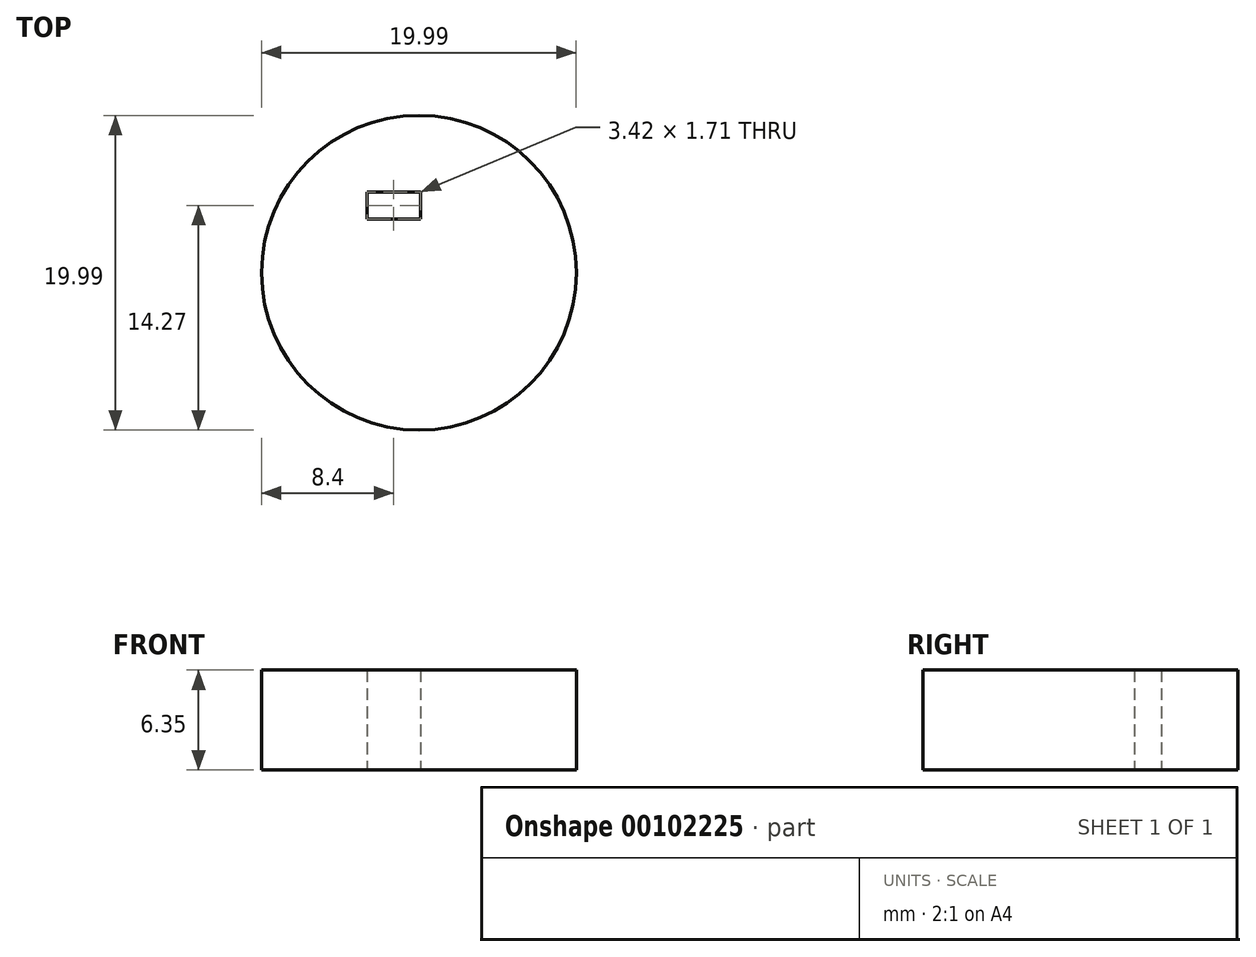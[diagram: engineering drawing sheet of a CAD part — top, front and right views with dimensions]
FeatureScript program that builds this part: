
annotation { "Feature Type Name" : "Feature", "Feature Type Description" : "" }
export const myFeature = defineFeature(function(context is Context, id is Id, definition is map)
    precondition{}
    {
        {
            var Q0;
            Q0=qCreatedBy(makeId("Top.planeOp"),FACE);
            var sketch = newSketch(context, id + "F0", { "sketchPlane" : qUnion([Q0])});
            skCircle(sketch, "E0", {"center": v(13, -19.54) * mm, "radius": 10 * mm});
            skLineSegment(sketch, "E1.bottom", {"start": v(9.7, -14.4) * mm, "end": v(13.12, -14.4) * mm});
            skLineSegment(sketch, "E1.top", {"start": v(9.7, -16.12) * mm, "end": v(13.12, -16.12) * mm});
            skLineSegment(sketch, "E1.left", {"start": v(9.7, -14.4) * mm, "end": v(9.7, -16.12) * mm});
            skLineSegment(sketch, "E1.right", {"start": v(13.12, -14.4) * mm, "end": v(13.12, -16.12) * mm});
            skSolve(sketch);
        }
        {
            var Q0;
            Q0=makeQuery(id+"F0.imprint","IMPRINT",FACE,{"disambiguationData":[TD([[makeQuery(id+"F0.imprint","IMPRINT",EDGE,{"derivedFrom":sQuery(id+"F0.wireOp",EDGE,"E0")}),1.0]])]});
            extrude(context, id + "F1", {"entities" : qUnion([Q0]), "depth" : 6.35 * mm});
        }
    });
